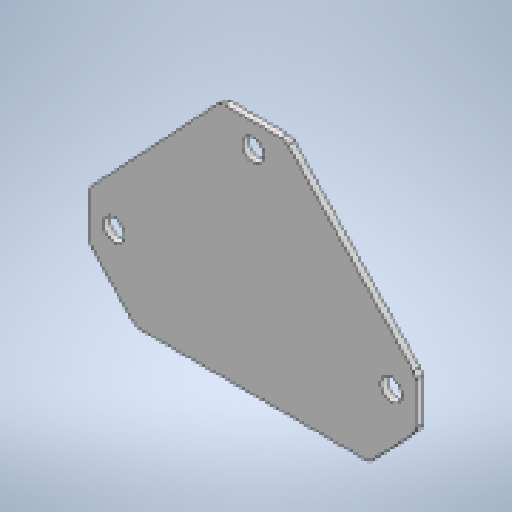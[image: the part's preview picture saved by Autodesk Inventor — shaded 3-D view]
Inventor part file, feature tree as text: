
AUTODESK INVENTOR PART (.ipt)
format: ipt  version: 2025 (Build 290162010, 162A)  size: 168,960 bytes
history: native  units: mm
features: sheet_metal_op x1, chamfer x1, sketch x1, other x1
ambient origin geometry x8: Origin, YZ Plane, XZ Plane, XY Plane, X Axis, Y Axis, Z Axis, Center Point
bodies: Solid1 (feature_tree)
feature tree (4):
  sheet_metal_op  "Face1"
  chamfer  "Corner Round2"
  sketch  "Sketch1"  dims[d2=80.0mm d3=80.0mm d6=4.0mm d17=5.0mm d18=13.0mm d19=45.0mm d20=45.0mm d21=40.0mm d22=15.0mm d23=15.0mm d24=30.0mm d25=6.0mm]
  other  "Plate1"
